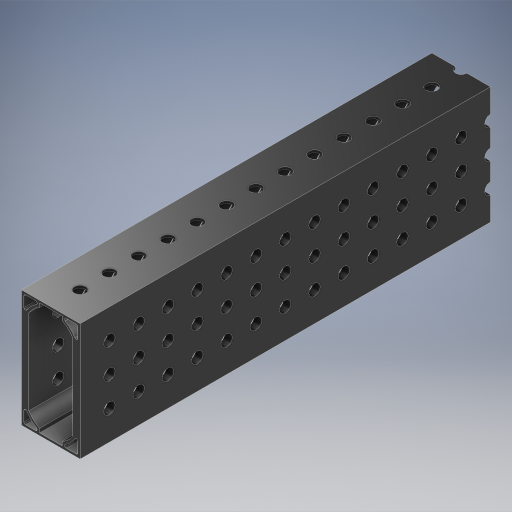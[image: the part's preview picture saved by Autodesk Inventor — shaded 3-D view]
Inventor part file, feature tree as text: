
AUTODESK INVENTOR PART (.ipt)
format: ipt  version: 2024.2 (Build 282272000, 272)  size: 908,800 bytes
history: native  units: in
note: dims shown in document units (in); Inventor stores cm internally (conversion verified against a paired STEP export)
features: other x13, extrude x9, hole x3, pattern_linear x3, mirror x3, sheet_metal_op x1, plane x1
ambient origin geometry x8: Origin, YZ Plane, XZ Plane, XY Plane, X Axis, Y Axis, Z Axis, Center Point
bodies: Solid1 (feature_tree)
feature tree (33):
  other  "MAXTube"
  other  "Blocks"
  other  "Base Sketch"
  extrude  "Base"  Depth=2.0in
  extrude  "MAX Corner"  Depth=1.0in
  extrude  "MAX Corner Cut"  Depth=0.125in
  extrude  "Scribe Lines"  Depth=0.04in
  other  "Side Middle"
  other  "Top Middle"
  other  "Side Holes Sketch"
  hole  "Top Side Hole"  [1 undecoded]
  hole  "Mid Side Hole"  [1 undecoded]
  hole  "Btm Side Hole"  [1 undecoded]
  pattern_linear  "Side Holes"  Spacing1=0.04in  [1 undecoded]
  mirror  "Side Mirror"
  extrude  "MAXTube Hole"  Depth=0.04in
  extrude  "MAXTube Outside"  Depth=7.0in
  pattern_linear  "MAXTube Pattern"  Spacing1=0.0in  [1 undecoded]
  mirror  "MAXTube Mirror"
  extrude  "Left Top Hole"  Depth=7.0in
  extrude  "Mid Top Hole"  TaperAngle=0.0deg  [1 undecoded]
  extrude  "Right Top Hole"  TaperAngle=0.0deg  [1 undecoded]
  pattern_linear  "Top Holes"  Spacing1=0.005in  [1 undecoded]
  mirror  "Top Mirror"
  sheet_metal_op  "Corner"
  plane  "Work Plane3"
  other  "Corner:5"
  other  "Corner:6"
  other  "Corner:7"
  other  "Corner:8"
  other  "MAXTube:1"
  other  "MAXTube:2"
  other  "MAXTube:3"
note: 8 required parameter values undecoded (feature->parameter linkage not recoverable at this tier; creation-order binding heuristic only, values carry confidence <= 0.55)
